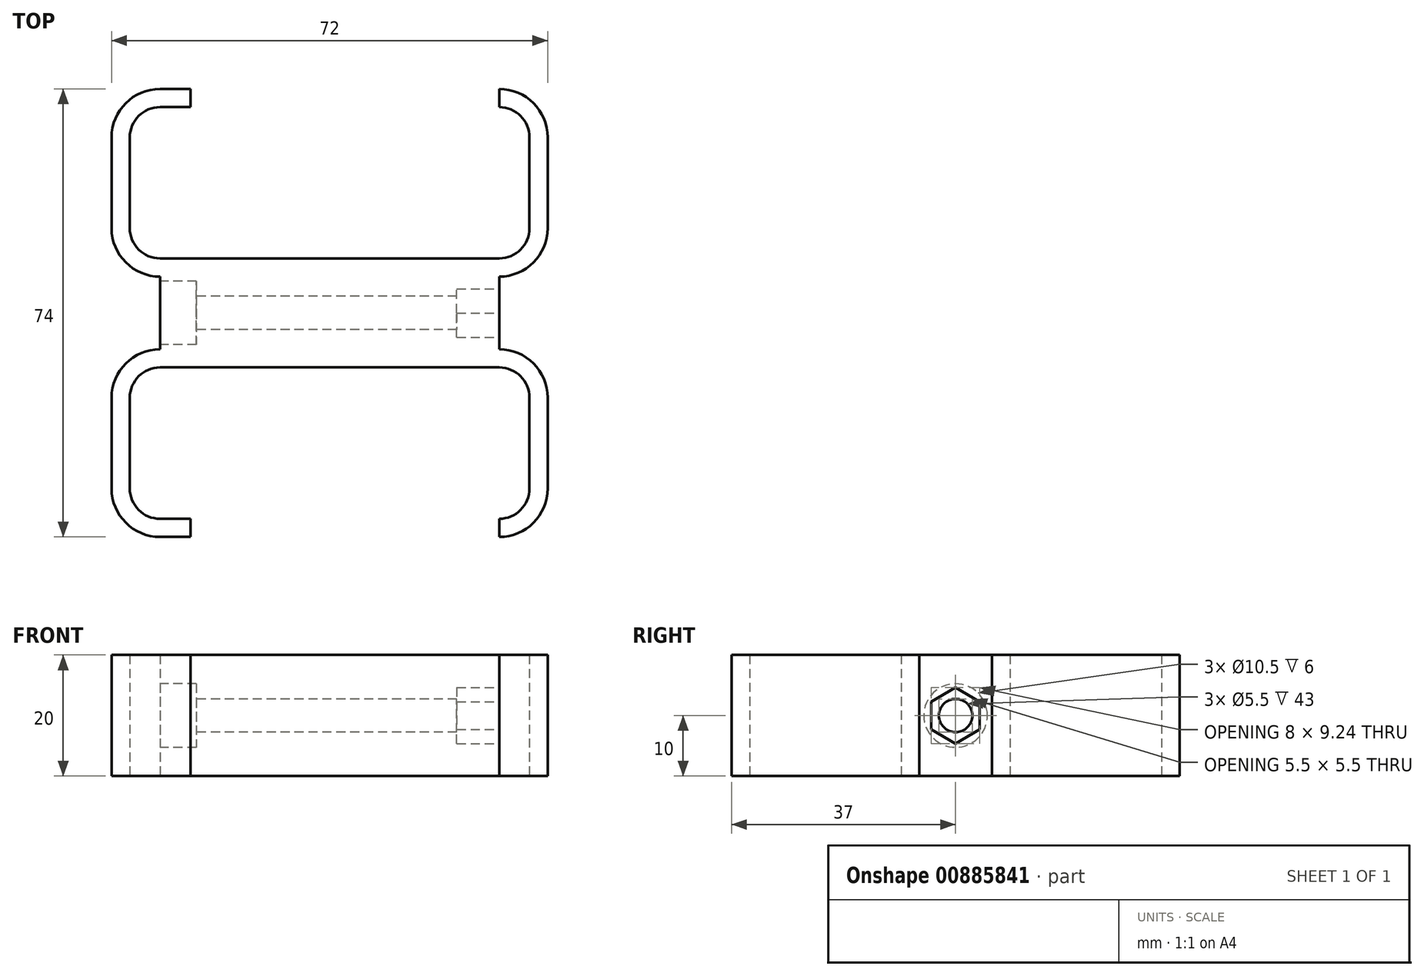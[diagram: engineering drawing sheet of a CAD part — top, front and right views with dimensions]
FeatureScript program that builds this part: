
annotation { "Feature Type Name" : "Feature", "Feature Type Description" : "" }
export const myFeature = defineFeature(function(context is Context, id is Id, definition is map)
    precondition{}
    {
        {
            var Q0;
            Q0=qCreatedBy(makeId("Top.planeOp"),FACE);
            var sketch = newSketch(context, id + "F0", { "sketchPlane" : qUnion([Q0])});
            skLineSegment(sketch, "E0", {"start": v(-10, 5) * mm, "end": v(-10, 20) * mm});
            skLineSegment(sketch, "E1", {"start": v(-5, 25) * mm, "end": v(51, 25) * mm});
            skLineSegment(sketch, "E2", {"start": v(56, 20) * mm, "end": v(56, 5) * mm});
            skLineSegment(sketch, "E3", {"start": v(51, 0) * mm, "end": v(46, 0) * mm});
            skLineSegment(sketch, "E4", {"start": v(-5, 0) * mm, "end": v(0, 0) * mm});
            skPoint(sketch, "E5.visualSharp", {"position": v(-10, 0) * mm});
            skArc(sketch, "E5.filletArc", {"start": v(-10, 5) * mm, "mid": v(-8.54, 1.46) * mm, "end": v(-5, 0) * mm});
            skPoint(sketch, "E6.visualSharp", {"position": v(-10, 25) * mm});
            skArc(sketch, "E6.filletArc", {"start": v(-5, 25) * mm, "mid": v(-8.54, 23.54) * mm, "end": v(-10, 20) * mm});
            skPoint(sketch, "E7.visualSharp", {"position": v(56, 25) * mm});
            skArc(sketch, "E7.filletArc", {"start": v(56, 20) * mm, "mid": v(54.54, 23.54) * mm, "end": v(51, 25) * mm});
            skPoint(sketch, "E8.visualSharp", {"position": v(56, 0) * mm});
            skArc(sketch, "E8.filletArc", {"start": v(51, 0) * mm, "mid": v(54.54, 1.46) * mm, "end": v(56, 5) * mm});
            skLineSegment(sketch, "E9.0", {"start": v(-5, -3) * mm, "end": v(0, -3) * mm});
            skArc(sketch, "E9.1", {"start": v(-13, 5) * mm, "mid": v(-10.66, -0.66) * mm, "end": v(-5, -3) * mm});
            skLineSegment(sketch, "E9.2", {"start": v(-13, 5) * mm, "end": v(-13, 20) * mm});
            skArc(sketch, "E9.3", {"start": v(-5, 28) * mm, "mid": v(-10.66, 25.66) * mm, "end": v(-13, 20) * mm});
            skArc(sketch, "E9.4", {"start": v(51, -3) * mm, "mid": v(56.66, -0.66) * mm, "end": v(59, 5) * mm});
            skLineSegment(sketch, "E9.5", {"start": v(59, 20) * mm, "end": v(59, 5) * mm});
            skArc(sketch, "E9.6", {"start": v(59, 20) * mm, "mid": v(56.66, 25.66) * mm, "end": v(51, 28) * mm});
            skLineSegment(sketch, "E9.7", {"start": v(-5, 28) * mm, "end": v(51, 28) * mm, "construction": true});
            skLineSegment(sketch, "E10", {"start": v(0, 0) * mm, "end": v(0, -3) * mm});
            skLineSegment(sketch, "E11", {"start": v(51, 0) * mm, "end": v(51, -3) * mm});
            skLineSegment(sketch, "E12", {"start": v(23, 28) * mm, "end": v(23, 40) * mm, "construction": true});
            skLineSegment(sketch, "E13", {"start": v(23, 34) * mm, "end": v(32.37, 34) * mm, "construction": true});
            skLineSegment(sketch, "E14.MirrorCS", {"start": v(-5, 43) * mm, "end": v(51, 43) * mm});
            skArc(sketch, "E15.MirrorCS", {"start": v(-5, 40) * mm, "mid": v(-10.66, 42.34) * mm, "end": v(-13, 48) * mm});
            skArc(sketch, "E16.MirrorCS", {"start": v(-5, 43) * mm, "mid": v(-8.54, 44.46) * mm, "end": v(-10, 48) * mm});
            skLineSegment(sketch, "E17.MirrorCS", {"start": v(-13, 63) * mm, "end": v(-13, 48) * mm});
            skLineSegment(sketch, "E18.MirrorCS", {"start": v(-10, 63) * mm, "end": v(-10, 48) * mm});
            skArc(sketch, "E19.MirrorCS", {"start": v(-13, 63) * mm, "mid": v(-10.66, 68.66) * mm, "end": v(-5, 71) * mm});
            skArc(sketch, "E20.MirrorCS", {"start": v(-10, 63) * mm, "mid": v(-8.54, 66.54) * mm, "end": v(-5, 68) * mm});
            skLineSegment(sketch, "E21.MirrorCS", {"start": v(-5, 68) * mm, "end": v(0, 68) * mm});
            skLineSegment(sketch, "E22.MirrorCS", {"start": v(-5, 71) * mm, "end": v(0, 71) * mm});
            skLineSegment(sketch, "E23.MirrorCS", {"start": v(0, 68) * mm, "end": v(0, 71) * mm});
            skLineSegment(sketch, "E24.MirrorCS", {"start": v(51, 68) * mm, "end": v(51, 71) * mm});
            skArc(sketch, "E25.MirrorCS", {"start": v(51, 71) * mm, "mid": v(56.66, 68.66) * mm, "end": v(59, 63) * mm});
            skArc(sketch, "E26.MirrorCS", {"start": v(51, 68) * mm, "mid": v(54.54, 66.54) * mm, "end": v(56, 63) * mm});
            skLineSegment(sketch, "E27.MirrorCS", {"start": v(56, 48) * mm, "end": v(56, 63) * mm});
            skLineSegment(sketch, "E28.MirrorCS", {"start": v(59, 48) * mm, "end": v(59, 63) * mm});
            skArc(sketch, "E29.MirrorCS", {"start": v(59, 48) * mm, "mid": v(56.66, 42.34) * mm, "end": v(51, 40) * mm});
            skArc(sketch, "E30.MirrorCS", {"start": v(56, 48) * mm, "mid": v(54.54, 44.46) * mm, "end": v(51, 43) * mm});
            skLineSegment(sketch, "E31.MirrorCS", {"start": v(-5, 40) * mm, "end": v(51, 40) * mm, "construction": true});
            skLineSegment(sketch, "E32", {"start": v(-5, 40) * mm, "end": v(-5, 28) * mm});
            skLineSegment(sketch, "E33", {"start": v(51, 40) * mm, "end": v(51, 28) * mm});
            skSolve(sketch);
        }
        {
            var Q0;
            Q0 = qSketchRegion(id + "F0", true);
            extrude(context, id + "F1", {"entities" : qUnion([Q0]), "depth" : 20 * mm, "offsetDistance" : 25 * mm});
        }
        {
            var Q0;
            Q0=makeQuery(id+"F1.opExtrude","SWEPT_FACE",FACE,{"disambiguationData":[OSD([sQuery(id+"F0.wireOp",EDGE,"E32")])]});
            var sketch = newSketch(context, id + "F2", { "sketchPlane" : qUnion([Q0])});
            skLineSegment(sketch, "E34", {"start": v(-40, 20) * mm, "end": v(-28, 0) * mm, "construction": true});
            skLineSegment(sketch, "E35", {"start": v(-28, 20) * mm, "end": v(-40, 0) * mm, "construction": true});
            skPoint(sketch, "E36", {"position": v(-34, 10) * mm});
            skCircle(sketch, "E37", {"center": v(-34, 10) * mm, "radius": 5.25 * mm});
            skSolve(sketch);
        }
        {
            var Q0;
            Q0 = qSketchRegion(id + "F2", true);
            extrude(context, id + "F3", {"entities" : qUnion([Q0]), "operationType" : NewBodyOperationType.REMOVE, "oppositeDirection" : true, "depth" : 6 * mm, "offsetDistance" : 25 * mm});
        }
        {
            var Q0;
            Q0=makeQuery(id+"F1.opExtrude","SWEPT_FACE",FACE,{"disambiguationData":[OSD([sQuery(id+"F0.wireOp",EDGE,"E33")])]});
            var sketch = newSketch(context, id + "F4", { "sketchPlane" : qUnion([Q0])});
            skLineSegment(sketch, "E38", {"start": v(28, 20) * mm, "end": v(40, 0) * mm, "construction": true});
            skLineSegment(sketch, "E39", {"start": v(40, 0) * mm, "end": v(40, 20) * mm, "construction": true});
            skLineSegment(sketch, "E40", {"start": v(40, 20) * mm, "end": v(28, 0) * mm, "construction": true});
            skPoint(sketch, "E41", {"position": v(34, 10) * mm});
            skCircle(sketch, "E42.cCircle", {"center": v(34, 10) * mm, "radius": 4 * mm, "construction": true});
            skLineSegment(sketch, "E42.0", {"start": v(38, 12.3) * mm, "end": v(38, 7.7) * mm});
            skLineSegment(sketch, "E42.1", {"start": v(38, 7.7) * mm, "end": v(34, 5.38) * mm});
            skLineSegment(sketch, "E42.2", {"start": v(34, 5.38) * mm, "end": v(30, 7.7) * mm});
            skLineSegment(sketch, "E42.3", {"start": v(30, 7.7) * mm, "end": v(30, 12.3) * mm});
            skLineSegment(sketch, "E42.4", {"start": v(30, 12.3) * mm, "end": v(34, 14.62) * mm});
            skLineSegment(sketch, "E42.5", {"start": v(34, 14.62) * mm, "end": v(38, 12.3) * mm});
            skPoint(sketch, "E42.0.midPoint", {"position": v(38, 10) * mm});
            skSolve(sketch);
        }
        {
            var Q0;
            Q0 = qSketchRegion(id + "F4", true);
            extrude(context, id + "F5", {"entities" : qUnion([Q0]), "operationType" : NewBodyOperationType.REMOVE, "oppositeDirection" : true, "depth" : 7 * mm, "offsetDistance" : 25 * mm});
        }
        {
            var Q0;
            Q0=makeQuery(id+"F3.boolean.opBoolean","COPY",FACE,{"derivedFrom":makeQuery(id+"F3.opExtrude","CAP_FACE",FACE,{"disambiguationData":[OSD([sQuery(id+"F2.wireOp",EDGE,"E37")])],"isStart":false})});
            var sketch = newSketch(context, id + "F6", { "sketchPlane" : qUnion([Q0])});
            skCircle(sketch, "E43", {"center": v(-34, 10) * mm, "radius": 2.75 * mm});
            skSolve(sketch);
        }
        {
            var Q0;
            Q0 = qSketchRegion(id + "F6", true);
            extrude(context, id + "F7", {"entities" : qUnion([Q0]), "operationType" : NewBodyOperationType.REMOVE, "endBound" : BoundingType.THROUGH_ALL, "oppositeDirection" : true, "depth" : 25 * mm, "offsetDistance" : 25 * mm});
        }
    });
